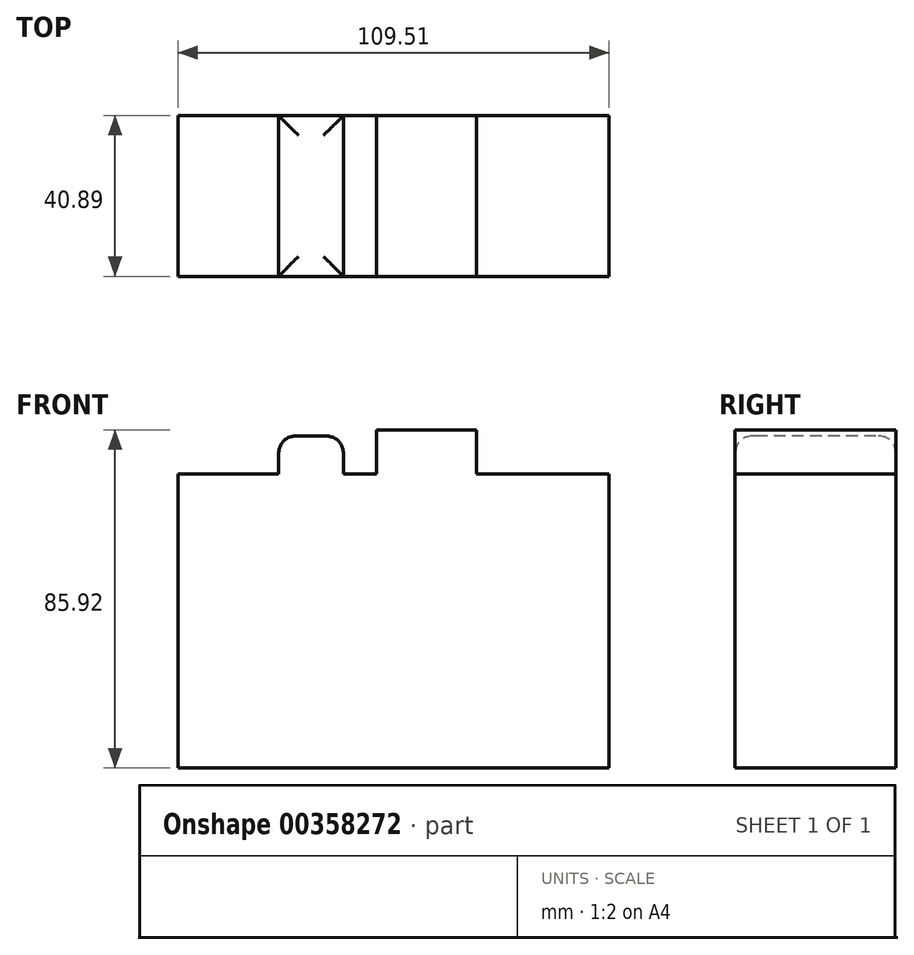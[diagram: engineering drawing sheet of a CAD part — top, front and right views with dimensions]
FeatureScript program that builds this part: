
annotation { "Feature Type Name" : "Feature", "Feature Type Description" : "" }
export const myFeature = defineFeature(function(context is Context, id is Id, definition is map)
    precondition{}
    {
        {
            var Q0;
            Q0=qCreatedBy(makeId("Front.planeOp"),FACE);
            var sketch = newSketch(context, id + "F0", { "sketchPlane" : qUnion([Q0])});
            skLineSegment(sketch, "E0.bottom", {"start": v(-44.77, -35.15) * mm, "end": v(64.74, -35.15) * mm});
            skLineSegment(sketch, "E0.top", {"start": v(-44.77, 39.53) * mm, "end": v(-19.26, 39.53) * mm});
            skLineSegment(sketch, "E0.left", {"start": v(-44.77, -35.15) * mm, "end": v(-44.77, 39.53) * mm});
            skLineSegment(sketch, "E0.right", {"start": v(64.74, -35.15) * mm, "end": v(64.74, 39.53) * mm});
            skLineSegment(sketch, "E1.top", {"start": v(-2.77, 49.25) * mm, "end": v(-19.26, 49.25) * mm});
            skLineSegment(sketch, "E1.left", {"start": v(-2.77, 39.53) * mm, "end": v(-2.77, 49.25) * mm});
            skLineSegment(sketch, "E1.right", {"start": v(-19.26, 39.53) * mm, "end": v(-19.26, 49.25) * mm});
            skLineSegment(sketch, "E2.trimOffspring", {"start": v(-2.77, 39.53) * mm, "end": v(5.59, 39.53) * mm});
            skLineSegment(sketch, "E3.bottom", {"start": v(5.59, 50.77) * mm, "end": v(30.99, 50.77) * mm});
            skLineSegment(sketch, "E3.left", {"start": v(5.59, 50.77) * mm, "end": v(5.59, 39.53) * mm});
            skLineSegment(sketch, "E3.right", {"start": v(30.99, 50.77) * mm, "end": v(30.99, 39.53) * mm});
            skLineSegment(sketch, "E4.trimOffspring", {"start": v(30.99, 39.53) * mm, "end": v(64.74, 39.53) * mm});
            skSolve(sketch);
        }
        {
            var Q0;
            Q0=makeQuery(id+"F0.imprint","IMPRINT",FACE,{"disambiguationData":[TD([[makeQuery(id+"F0.imprint","IMPRINT",EDGE,{"derivedFrom":sQuery(id+"F0.wireOp",EDGE,"E0.bottom")}),1.0]])]});
            extrude(context, id + "F1", {"entities" : qUnion([Q0]), "depth" : 40.9 * mm});
        }
        {
            var Q0;
            Q0=makeQuery(id+"F1.opExtrude","SWEPT_FACE",FACE,{"disambiguationData":[OSD([sQuery(id+"F0.wireOp",EDGE,"E1.top")])]});
            fillet(context, id + "F2", {"entities" : qUnion([Q0]), "radius" : 5.08 * mm, "tangentPropagation" : true, "rho" : 0.5, "crossSection" : FilletCrossSection.CONIC, "allowEdgeOverflow" : false});
        }
    });
